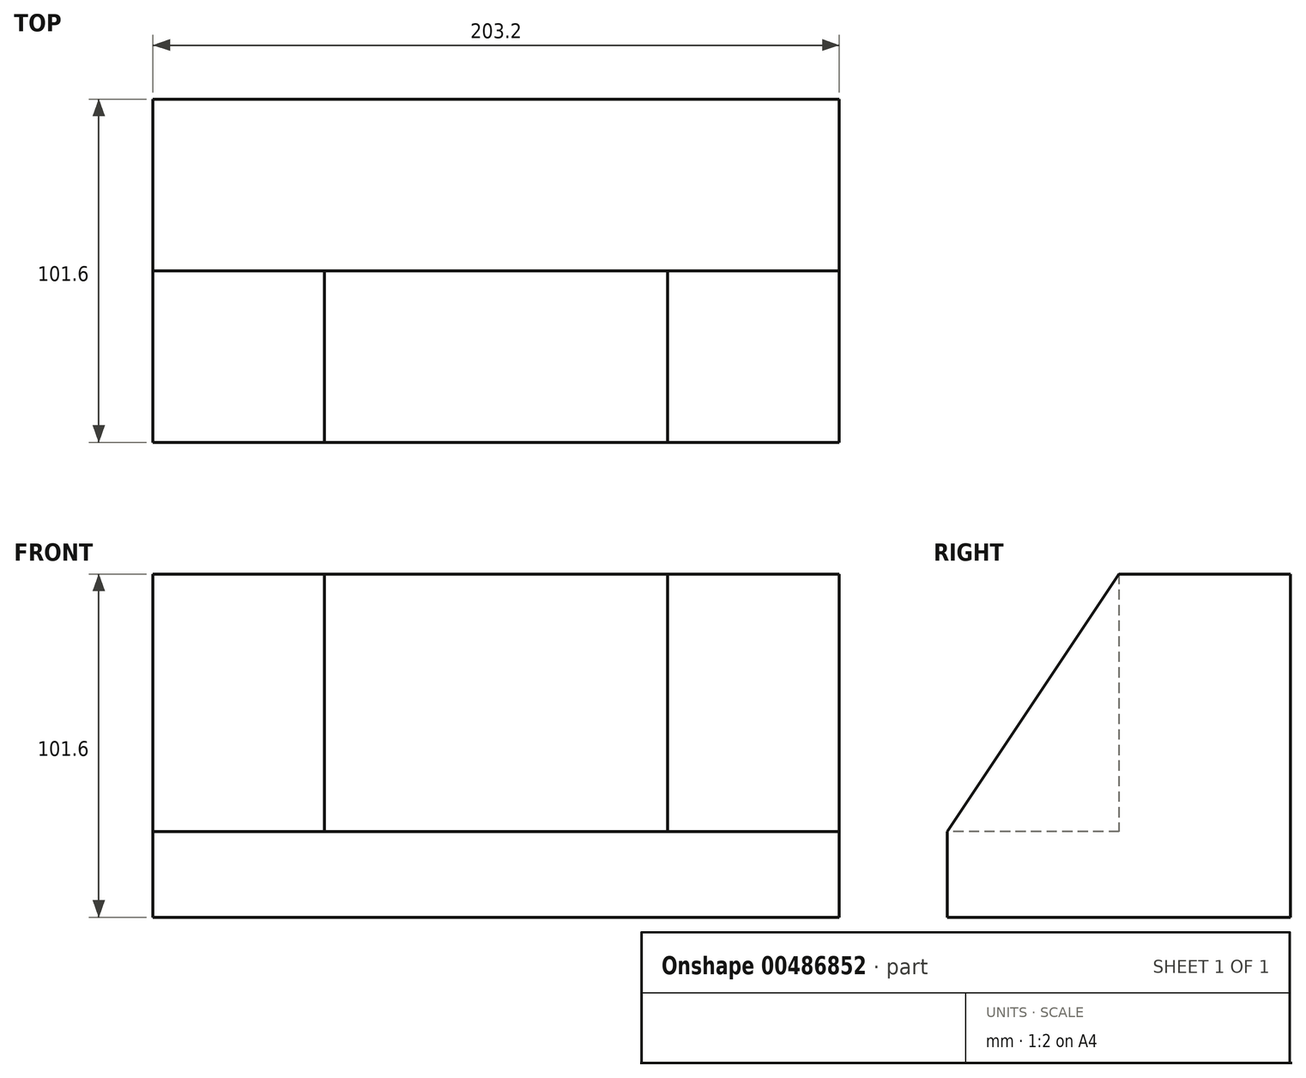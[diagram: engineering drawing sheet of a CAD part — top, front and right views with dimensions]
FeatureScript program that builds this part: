
annotation { "Feature Type Name" : "Feature", "Feature Type Description" : "" }
export const myFeature = defineFeature(function(context is Context, id is Id, definition is map)
    precondition{}
    {
        {
            var Q0;
            Q0=qCreatedBy(makeId("Top.planeOp"),FACE);
            var sketch = newSketch(context, id + "F0", { "sketchPlane" : qUnion([Q0])});
            skLineSegment(sketch, "E0.bottom", {"start": v(-101.6, 44.27) * mm, "end": v(0, 44.27) * mm});
            skLineSegment(sketch, "E0.top", {"start": v(-101.6, -6.53) * mm, "end": v(0, -6.53) * mm});
            skLineSegment(sketch, "E0.left", {"start": v(-101.6, 44.27) * mm, "end": v(-101.6, -6.53) * mm});
            skLineSegment(sketch, "E0.right", {"start": v(0, 44.27) * mm, "end": v(0, -6.53) * mm});
            skSolve(sketch);
        }
        {
            var Q0;
            Q0 = qSketchRegion(id + "F0", true);
            extrude(context, id + "F1", {"entities" : qUnion([Q0]), "depth" : 25.4 * mm});
        }
        {
            var Q0;
            Q0=makeQuery(id+"F1.opExtrude","SWEPT_FACE",FACE,{"disambiguationData":[OSD([sQuery(id+"F0.wireOp",EDGE,"E0.bottom")])]});
            var sketch = newSketch(context, id + "F2", { "sketchPlane" : qUnion([Q0])});
            skLineSegment(sketch, "E1.bottom", {"start": v(0, 0) * mm, "end": v(101.6, 0) * mm});
            skLineSegment(sketch, "E1.top", {"start": v(0, 101.6) * mm, "end": v(101.6, 101.6) * mm});
            skLineSegment(sketch, "E1.left", {"start": v(0, 0) * mm, "end": v(0, 101.6) * mm});
            skLineSegment(sketch, "E1.right", {"start": v(101.6, 0) * mm, "end": v(101.6, 101.6) * mm});
            skSolve(sketch);
        }
        {
            var Q0;
            Q0 = qSketchRegion(id + "F2", true);
            extrude(context, id + "F3", {"entities" : qUnion([Q0]), "operationType" : NewBodyOperationType.ADD, "depth" : 50.8 * mm});
        }
        {
            var Q0;
            Q0=makeQuery(id+"F3.boolean.opBoolean","MERGE",FACE,{"derivedFrom":[makeQuery(id+"F1.opExtrude","SWEPT_FACE",FACE,{"disambiguationData":[OSD([sQuery(id+"F0.wireOp",EDGE,"E0.right")])]}),makeQuery(id+"F3.opExtrude","SWEPT_FACE",FACE,{"disambiguationData":[OSD([sQuery(id+"F2.wireOp",EDGE,"E1.left")])]})]});
            var sketch = newSketch(context, id + "F4", { "sketchPlane" : qUnion([Q0])});
            skLineSegment(sketch, "E2.bottom", {"start": v(95.07, 0) * mm, "end": v(-6.53, 0) * mm});
            skLineSegment(sketch, "E2.top", {"start": v(95.07, 101.6) * mm, "end": v(-6.53, 101.6) * mm});
            skLineSegment(sketch, "E2.left", {"start": v(95.07, 0) * mm, "end": v(95.07, 101.6) * mm});
            skLineSegment(sketch, "E2.right", {"start": v(-6.53, 0) * mm, "end": v(-6.53, 101.6) * mm});
            skLineSegment(sketch, "E3", {"start": v(-6.53, 25.4) * mm, "end": v(44.27, 101.6) * mm});
            skSolve(sketch);
        }
        {
            var Q0;
            Q0=makeQuery(id+"F4.imprint","IMPRINT",FACE,{"disambiguationData":[TD([[makeQuery(id+"F4.imprint","IMPRINT",EDGE,{"derivedFrom":sQuery(id+"F4.wireOp",EDGE,"E3")}),-1.0]])]});
            var Q1;
            {var subQ5=sQuery(id+"F4.wireOp",EDGE,"E2.bottom");Q1=makeQuery(id+"F4.imprint","IMPRINT",FACE,{"disambiguationData":[TD([[makeQuery(id+"F4.imprint","IMPRINT",EDGE,{"derivedFrom":subQ5}),-1.0]])]});}
            extrude(context, id + "F5", {"entities" : qUnion([Q0, Q1]), "operationType" : NewBodyOperationType.ADD, "depth" : 50.8 * mm});
        }
        {
            var Q0;
            Q0=makeQuery(id+"F3.boolean.opBoolean","MERGE",FACE,{"derivedFrom":[makeQuery(id+"F1.opExtrude","SWEPT_FACE",FACE,{"disambiguationData":[OSD([sQuery(id+"F0.wireOp",EDGE,"E0.left")])]}),makeQuery(id+"F3.opExtrude","SWEPT_FACE",FACE,{"disambiguationData":[OSD([sQuery(id+"F2.wireOp",EDGE,"E1.right")])]})]});
            var sketch = newSketch(context, id + "F6", { "sketchPlane" : qUnion([Q0])});
            skLineSegment(sketch, "E4.bottom", {"start": v(-95.07, 0) * mm, "end": v(6.53, 0) * mm});
            skLineSegment(sketch, "E4.top", {"start": v(-95.07, 101.6) * mm, "end": v(6.53, 101.6) * mm});
            skLineSegment(sketch, "E4.left", {"start": v(-95.07, 0) * mm, "end": v(-95.07, 101.6) * mm});
            skLineSegment(sketch, "E4.right", {"start": v(6.53, 0) * mm, "end": v(6.53, 101.6) * mm});
            skLineSegment(sketch, "E5", {"start": v(6.53, 25.4) * mm, "end": v(-44.27, 101.6) * mm});
            skSolve(sketch);
        }
        {
            var Q0;
            {var subQ5=sQuery(id+"F6.wireOp",EDGE,"E4.bottom");Q0=makeQuery(id+"F6.imprint","IMPRINT",FACE,{"disambiguationData":[TD([[makeQuery(id+"F6.imprint","IMPRINT",EDGE,{"derivedFrom":subQ5}),1.0]])]});}
            var Q1;
            Q1=makeQuery(id+"F6.imprint","IMPRINT",FACE,{"disambiguationData":[TD([[makeQuery(id+"F6.imprint","IMPRINT",EDGE,{"derivedFrom":sQuery(id+"F6.wireOp",EDGE,"E5")}),1.0]])]});
            extrude(context, id + "F7", {"entities" : qUnion([Q0, Q1]), "operationType" : NewBodyOperationType.ADD, "depth" : 50.8 * mm});
        }
    });
